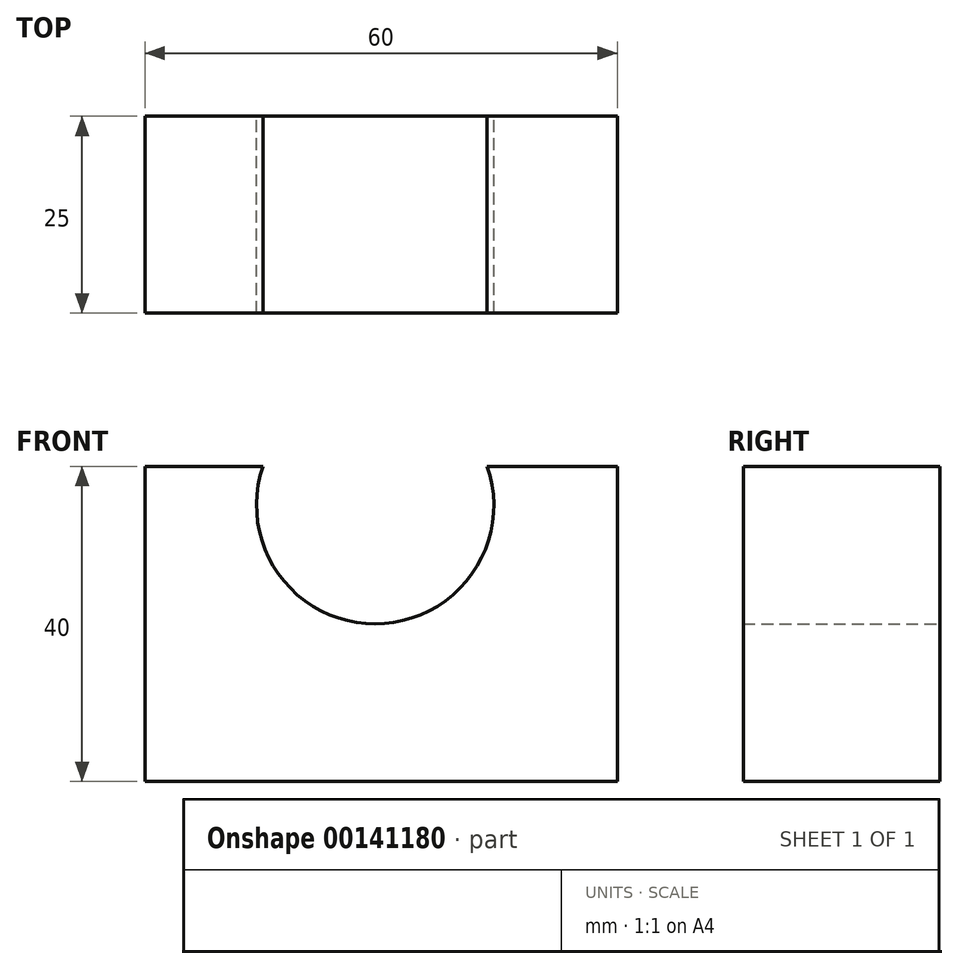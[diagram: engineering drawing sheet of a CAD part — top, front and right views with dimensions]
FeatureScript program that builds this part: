
annotation { "Feature Type Name" : "Feature", "Feature Type Description" : "" }
export const myFeature = defineFeature(function(context is Context, id is Id, definition is map)
    precondition{}
    {
        {
            var Q0;
            Q0=qCreatedBy(makeId("Front.planeOp"),FACE);
            var sketch = newSketch(context, id + "F0", { "sketchPlane" : qUnion([Q0])});
            skLineSegment(sketch, "E0", {"start": v(-29.85, 0) * mm, "end": v(30.15, 0) * mm});
            skLineSegment(sketch, "E1", {"start": v(30.15, 0) * mm, "end": v(30.15, 40) * mm});
            skLineSegment(sketch, "E2", {"start": v(30.15, 40) * mm, "end": v(13.62, 40) * mm});
            skLineSegment(sketch, "E3", {"start": v(-29.85, 0) * mm, "end": v(-29.85, 40) * mm});
            skLineSegment(sketch, "E4", {"start": v(-29.85, 40) * mm, "end": v(-14.85, 40) * mm});
            skArc(sketch, "E5", {"start": v(-14.85, 40) * mm, "mid": v(-0.62, 20) * mm, "end": v(13.62, 40) * mm});
            skLineSegment(sketch, "E6", {"start": v(-29.85, 20) * mm, "end": v(30.15, 20) * mm});
            skLineSegment(sketch, "E7", {"start": v(30.15, 20) * mm, "end": v(29.72, 20.38) * mm});
            skLineSegment(sketch, "E8", {"start": v(-9.85, 20) * mm, "end": v(-9.85, 0) * mm});
            skLineSegment(sketch, "E9", {"start": v(10.15, 20) * mm, "end": v(10.15, 0) * mm});
            skLineSegment(sketch, "E10", {"start": v(-29.85, 10) * mm, "end": v(30.15, 10) * mm, "construction": true});
            skSolve(sketch);
        }
        {
            var Q0;
            Q0 = qSketchRegion(id + "F0", true);
            extrude(context, id + "F1", {"entities" : qUnion([Q0]), "endBound" : BoundingType.SYMMETRIC, "depth" : 25 * mm});
        }
    });
